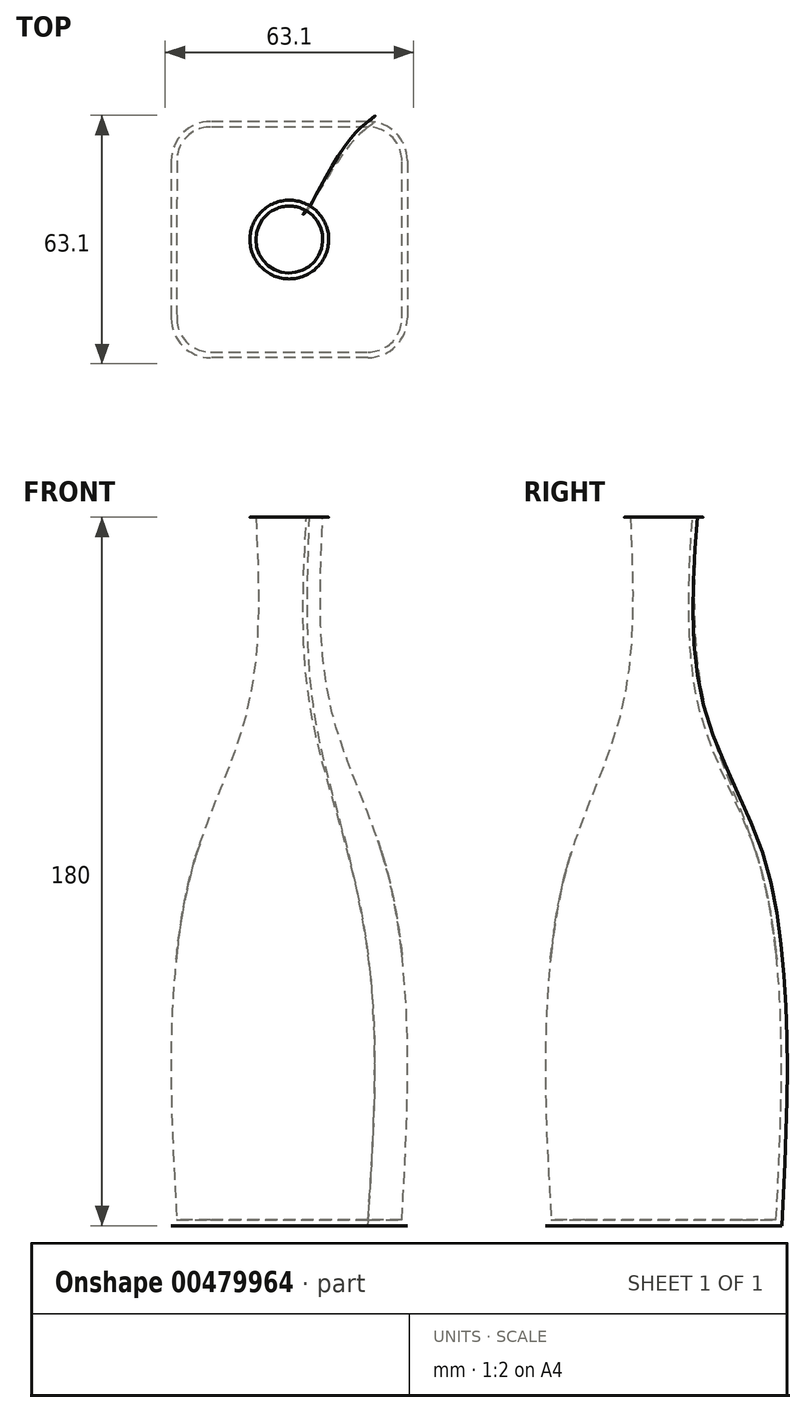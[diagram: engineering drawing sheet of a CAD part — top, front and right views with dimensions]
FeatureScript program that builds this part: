
annotation { "Feature Type Name" : "Feature", "Feature Type Description" : "" }
export const myFeature = defineFeature(function(context is Context, id is Id, definition is map)
    precondition{}
    {
        {
            var Q0;
            Q0=qCreatedBy(makeId("Top.planeOp"),FACE);
            var sketch = newSketch(context, id + "F0", { "sketchPlane" : qUnion([Q0])});
            skLineSegment(sketch, "E0.bottom", {"start": v(20, 30) * mm, "end": v(-20, 30) * mm});
            skLineSegment(sketch, "E0.top", {"start": v(20, -30) * mm, "end": v(-20, -30) * mm});
            skLineSegment(sketch, "E0.left", {"start": v(30, 20) * mm, "end": v(30, -20) * mm});
            skLineSegment(sketch, "E0.right", {"start": v(-30, 20) * mm, "end": v(-30, -20) * mm});
            skPoint(sketch, "E0.middle", {"position": v(0, 0) * mm});
            skPoint(sketch, "E1.visualSharp", {"position": v(-30, -30) * mm});
            skArc(sketch, "E1.filletArc", {"start": v(-30, -20) * mm, "mid": v(-27.07, -27.07) * mm, "end": v(-20, -30) * mm});
            skPoint(sketch, "E2.visualSharp", {"position": v(30, -30) * mm});
            skArc(sketch, "E2.filletArc", {"start": v(20, -30) * mm, "mid": v(27.07, -27.07) * mm, "end": v(30, -20) * mm});
            skPoint(sketch, "E3.visualSharp", {"position": v(30, 30) * mm});
            skArc(sketch, "E3.filletArc", {"start": v(30, 20) * mm, "mid": v(27.07, 27.07) * mm, "end": v(20, 30) * mm});
            skPoint(sketch, "E4.visualSharp", {"position": v(-30, 30) * mm});
            skArc(sketch, "E4.filletArc", {"start": v(-20, 30) * mm, "mid": v(-27.07, 27.07) * mm, "end": v(-30, 20) * mm});
            skSolve(sketch);
        }
        {
            var Q0;
            Q0=qCreatedBy(makeId("Top.planeOp"),FACE);
            cPlane(context, id + "F1", {"entities" : qUnion([Q0]), "cplaneType" : CPlaneType.OFFSET, "offset" : 70 * mm, "width" : 150 * mm, "height" : 150 * mm});
        }
        {
            var Q0;
            Q0=qCreatedBy(id+"F1.planeOp",FACE);
            var sketch = newSketch(context, id + "F2", { "sketchPlane" : qUnion([Q0])});
            skLineSegment(sketch, "E5.bottom", {"start": v(20, 30) * mm, "end": v(-20, 30) * mm});
            skLineSegment(sketch, "E5.top", {"start": v(20, -30) * mm, "end": v(-20, -30) * mm});
            skLineSegment(sketch, "E5.left", {"start": v(30, 20) * mm, "end": v(30, -20) * mm});
            skLineSegment(sketch, "E5.right", {"start": v(-30, 20) * mm, "end": v(-30, -20) * mm});
            skPoint(sketch, "E5.middle", {"position": v(0, 0) * mm});
            skPoint(sketch, "E6.visualSharp", {"position": v(-30, 30) * mm});
            skArc(sketch, "E6.filletArc", {"start": v(-20, 30) * mm, "mid": v(-27.07, 27.07) * mm, "end": v(-30, 20) * mm});
            skPoint(sketch, "E7.visualSharp", {"position": v(30, 30) * mm});
            skArc(sketch, "E7.filletArc", {"start": v(30, 20) * mm, "mid": v(27.07, 27.07) * mm, "end": v(20, 30) * mm});
            skPoint(sketch, "E8.visualSharp", {"position": v(30, -30) * mm});
            skArc(sketch, "E8.filletArc", {"start": v(20, -30) * mm, "mid": v(27.07, -27.07) * mm, "end": v(30, -20) * mm});
            skPoint(sketch, "E9.visualSharp", {"position": v(-30, -30) * mm});
            skArc(sketch, "E9.filletArc", {"start": v(-30, -20) * mm, "mid": v(-27.07, -27.07) * mm, "end": v(-20, -30) * mm});
            skSolve(sketch);
        }
        {
            var Q0;
            Q0=qCreatedBy(id+"F1.planeOp",FACE);
            cPlane(context, id + "F3", {"entities" : qUnion([Q0]), "cplaneType" : CPlaneType.OFFSET, "offset" : 25 * mm, "width" : 150 * mm, "height" : 150 * mm});
        }
        {
            var Q0;
            Q0=qCreatedBy(id+"F3.planeOp",FACE);
            var sketch = newSketch(context, id + "F4", { "sketchPlane" : qUnion([Q0])});
            skLineSegment(sketch, "E10.bottom", {"start": v(15, 25) * mm, "end": v(-15, 25) * mm});
            skLineSegment(sketch, "E10.top", {"start": v(15, -25) * mm, "end": v(-15, -25) * mm});
            skLineSegment(sketch, "E10.left", {"start": v(25, 15) * mm, "end": v(25, -15) * mm});
            skLineSegment(sketch, "E10.right", {"start": v(-25, 15) * mm, "end": v(-25, -15) * mm});
            skPoint(sketch, "E10.middle", {"position": v(0, 0) * mm});
            skPoint(sketch, "E11.visualSharp", {"position": v(-25, 25) * mm});
            skArc(sketch, "E11.filletArc", {"start": v(-15, 25) * mm, "mid": v(-22.07, 22.07) * mm, "end": v(-25, 15) * mm});
            skPoint(sketch, "E12.visualSharp", {"position": v(25, 25) * mm});
            skArc(sketch, "E12.filletArc", {"start": v(25, 15) * mm, "mid": v(22.07, 22.07) * mm, "end": v(15, 25) * mm});
            skPoint(sketch, "E13.visualSharp", {"position": v(25, -25) * mm});
            skArc(sketch, "E13.filletArc", {"start": v(15, -25) * mm, "mid": v(22.07, -22.07) * mm, "end": v(25, -15) * mm});
            skPoint(sketch, "E14.visualSharp", {"position": v(-25, -25) * mm});
            skArc(sketch, "E14.filletArc", {"start": v(-25, -15) * mm, "mid": v(-22.07, -22.07) * mm, "end": v(-15, -25) * mm});
            skSolve(sketch);
        }
        {
            var Q0;
            Q0=qCreatedBy(id+"F3.planeOp",FACE);
            cPlane(context, id + "F5", {"entities" : qUnion([Q0]), "cplaneType" : CPlaneType.OFFSET, "offset" : 35 * mm, "width" : 150 * mm, "height" : 150 * mm});
        }
        {
            var Q0;
            Q0=qCreatedBy(id+"F5.planeOp",FACE);
            var sketch = newSketch(context, id + "F6", { "sketchPlane" : qUnion([Q0])});
            skCircle(sketch, "E15", {"center": v(0, 0) * mm, "radius": 12.5 * mm});
            skSolve(sketch);
        }
        {
            var Q0;
            Q0=qCreatedBy(id+"F5.planeOp",FACE);
            cPlane(context, id + "F7", {"entities" : qUnion([Q0]), "cplaneType" : CPlaneType.OFFSET, "offset" : 50 * mm, "width" : 150 * mm, "height" : 150 * mm});
        }
        {
            var Q0;
            Q0=qCreatedBy(id+"F7.planeOp",FACE);
            var sketch = newSketch(context, id + "F8", { "sketchPlane" : qUnion([Q0])});
            skCircle(sketch, "E16", {"center": v(0, 0) * mm, "radius": 10 * mm});
            skSolve(sketch);
        }
        {
            var Q0;
            Q0=makeQuery(id+"F0.imprint","IMPRINT",FACE,{"disambiguationData":[TD([[makeQuery(id+"F0.imprint","IMPRINT",EDGE,{"derivedFrom":sQuery(id+"F0.wireOp",EDGE,"E0.bottom")}),1.0]])]});
            var Q1;
            Q1=makeQuery(id+"F2.imprint","IMPRINT",FACE,{"disambiguationData":[TD([[makeQuery(id+"F2.imprint","IMPRINT",EDGE,{"derivedFrom":sQuery(id+"F2.wireOp",EDGE,"E5.bottom")}),1.0]])]});
            var Q2;
            Q2=makeQuery(id+"F4.imprint","IMPRINT",FACE,{"disambiguationData":[TD([[makeQuery(id+"F4.imprint","IMPRINT",EDGE,{"derivedFrom":sQuery(id+"F4.wireOp",EDGE,"E10.bottom")}),1.0]])]});
            var Q3;
            Q3=makeQuery(id+"F6.imprint","IMPRINT",FACE,{"disambiguationData":[TD([[makeQuery(id+"F6.imprint","IMPRINT",EDGE,{"derivedFrom":sQuery(id+"F6.wireOp",EDGE,"E15")}),1.0]])]});
            var Q4;
            Q4=makeQuery(id+"F8.imprint","IMPRINT",FACE,{"disambiguationData":[TD([[makeQuery(id+"F8.imprint","IMPRINT",EDGE,{"derivedFrom":sQuery(id+"F8.wireOp",EDGE,"E16")}),1.0]])]});
            loft(context, id + "F9", {"sheetProfilesArray" : [{ "sheetProfileEntities" : qUnion([Q0]) }, { "sheetProfileEntities" : qUnion([Q1]) }, { "sheetProfileEntities" : qUnion([Q2]) }, { "sheetProfileEntities" : qUnion([Q3]) }, { "sheetProfileEntities" : qUnion([Q4]) }]});
        }
        {
            var Q0;
            Q0=makeQuery(id+"F9.opLoft","CAP_FACE",FACE,{"disambiguationData":[OSD([makeQuery(id+"F8.imprint","IMPRINT",FACE,{"disambiguationData":[TD([[makeQuery(id+"F8.imprint","IMPRINT",EDGE,{"derivedFrom":sQuery(id+"F8.wireOp",EDGE,"E16")}),1.0]])]})])],"isStart":true});
            shell(context, id + "F10", {"entities" : qUnion([Q0]), "thickness" : 1.5 * mm});
        }
    });
